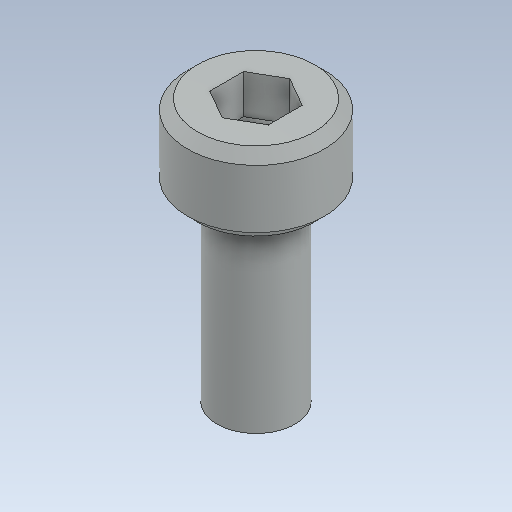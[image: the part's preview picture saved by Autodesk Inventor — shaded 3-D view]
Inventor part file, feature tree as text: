
AUTODESK INVENTOR PART (.ipt)
format: ipt  version: 2020 (Build 240168000, 168)  size: 111,104 bytes
history: native  units: in
note: dims shown in document units (in); Inventor stores cm internally (conversion verified against a paired STEP export)
features: chamfer x1
ambient origin geometry x8: Origin, YZ Plane, XZ Plane, XY Plane, X Axis, Y Axis, Z Axis, Center Point
bodies: Solid1 (feature_tree)
feature tree (1):
  chamfer  "Chamfer2"  [1 undecoded]
note: 1 required parameter value undecoded (feature->parameter linkage not recoverable at this tier; creation-order binding heuristic only, values carry confidence <= 0.55)
